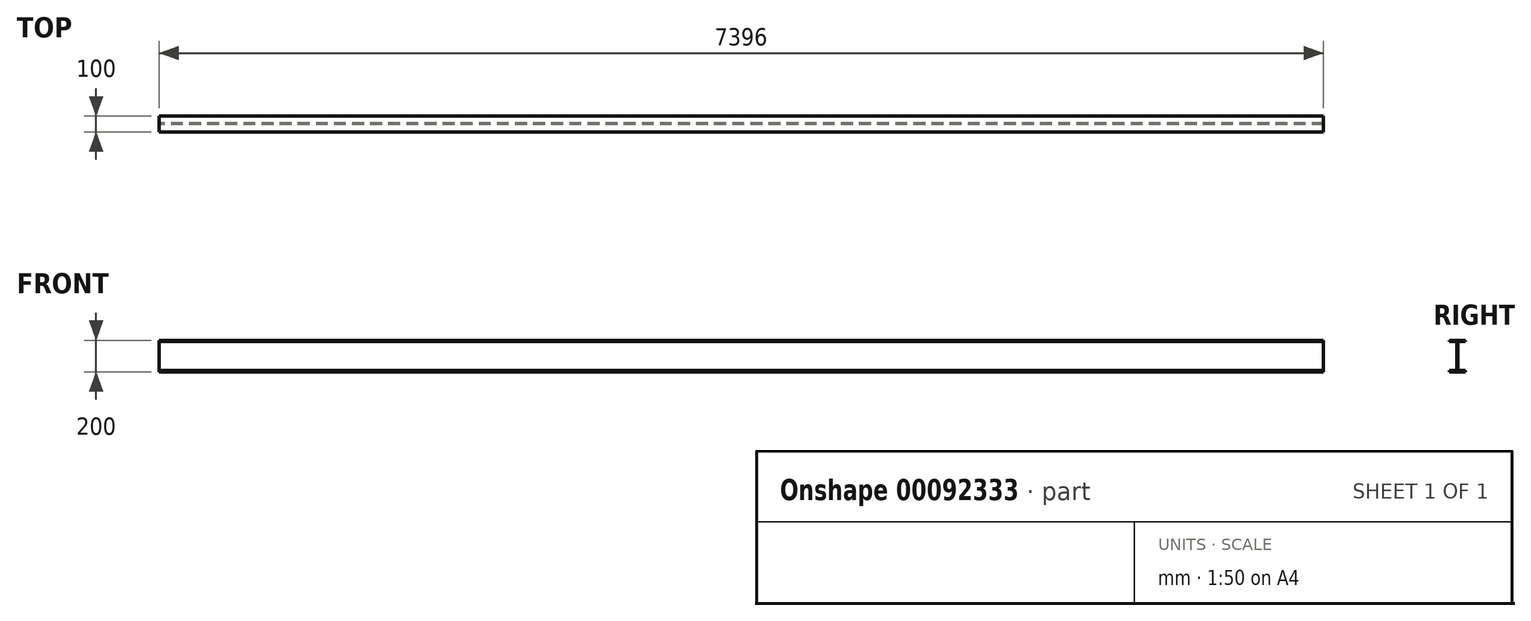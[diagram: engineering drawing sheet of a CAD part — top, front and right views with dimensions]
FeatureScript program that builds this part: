
annotation { "Feature Type Name" : "Feature", "Feature Type Description" : "" }
export const myFeature = defineFeature(function(context is Context, id is Id, definition is map)
    precondition{}
    {
        {
            var Q0;
            Q0=qCreatedBy(makeId("Right.planeOp"),FACE);
            var sketch = newSketch(context, id + "F0", { "sketchPlane" : qUnion([Q0])});
            skLineSegment(sketch, "E0", {"start": v(0, 0) * mm, "end": v(-100, 0) * mm});
            skLineSegment(sketch, "E1", {"start": v(-100, 200) * mm, "end": v(0, 200) * mm});
            skLineSegment(sketch, "E2", {"start": v(0, 200) * mm, "end": v(0, 192) * mm});
            skLineSegment(sketch, "E3", {"start": v(0, 192) * mm, "end": v(-46, 192) * mm});
            skLineSegment(sketch, "E4", {"start": v(-46, 192) * mm, "end": v(-46, 8) * mm});
            skLineSegment(sketch, "E5", {"start": v(-46, 8) * mm, "end": v(0, 8) * mm});
            skLineSegment(sketch, "E6", {"start": v(0, 8) * mm, "end": v(0, 0) * mm});
            skLineSegment(sketch, "E7", {"start": v(-100, 200) * mm, "end": v(-100, 192) * mm});
            skLineSegment(sketch, "E8", {"start": v(-100, 192) * mm, "end": v(-54, 192) * mm});
            skLineSegment(sketch, "E9", {"start": v(-54, 192) * mm, "end": v(-54, 8) * mm});
            skLineSegment(sketch, "E10", {"start": v(-54, 8) * mm, "end": v(-100, 8) * mm});
            skLineSegment(sketch, "E11", {"start": v(-100, 8) * mm, "end": v(-100, 0) * mm});
            skSolve(sketch);
        }
        {
            var Q0;
            Q0=qSketchRegion(id+"F0",true);
            extrude(context, id + "F1", {"entities" : qUnion([Q0]), "offsetDistance" : 25 * mm, "depth" : 7396 * mm});
        }
    });
